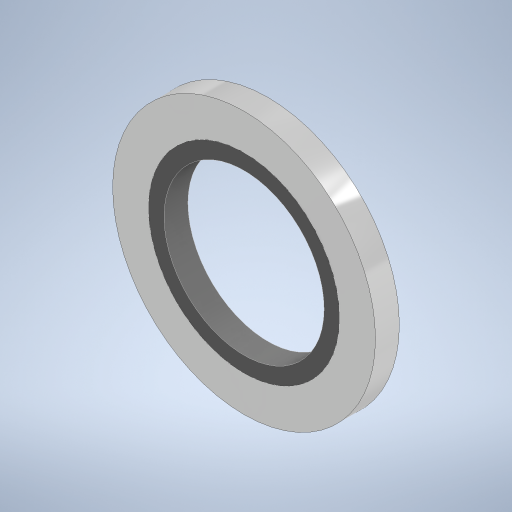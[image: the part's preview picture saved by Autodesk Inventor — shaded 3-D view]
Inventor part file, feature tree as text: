
AUTODESK INVENTOR PART (.ipt)
format: ipt  version: 2024.2 (Build 282272000, 272)  size: 255,488 bytes
history: native  units: mm
features: extrude x2, sketch x2
ambient origin geometry x8: Origin, YZ Plane, XZ Plane, XY Plane, X Axis, Y Axis, Z Axis, Center Point
bodies: Solid1 (feature_tree), Solid2 (feature_tree)
feature tree (4):
  extrude  "Extrusion1"  Depth=8.0mm
  extrude  "Extrusion2"  Depth=1.0mm
  sketch  "Sketch1"  dims[d0=11.0mm d1=8.0mm]
  sketch  "Sketch2"  dims[d2=1.0mm d3=0.0mm d4=6.7mm d5=1.0mm d6=0.0mm]
